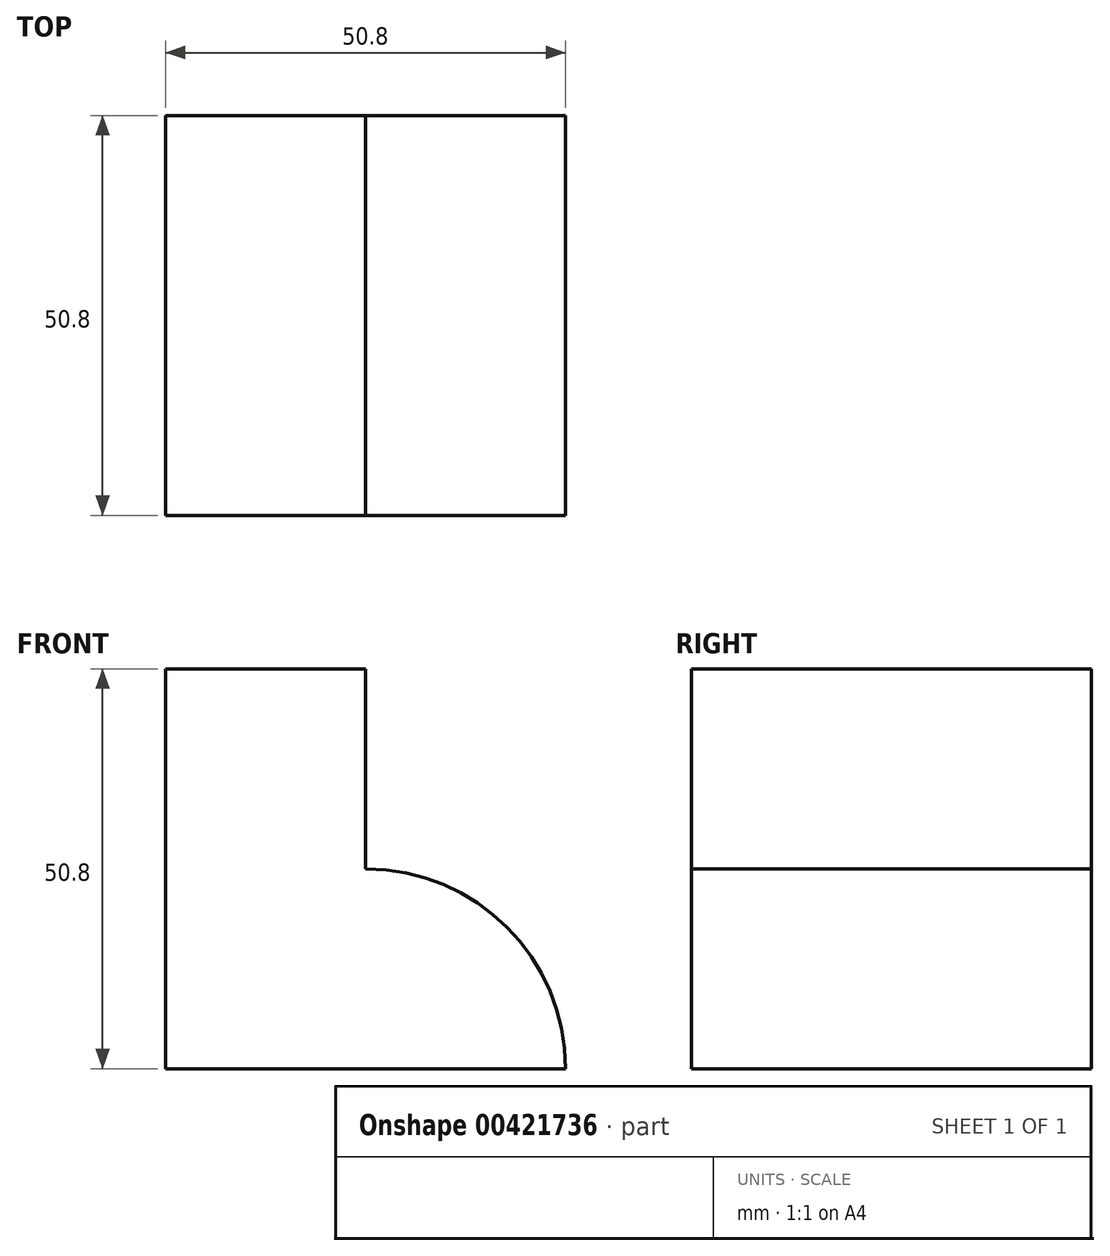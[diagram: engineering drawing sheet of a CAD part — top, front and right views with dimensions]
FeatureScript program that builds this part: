
annotation { "Feature Type Name" : "Feature", "Feature Type Description" : "" }
export const myFeature = defineFeature(function(context is Context, id is Id, definition is map)
    precondition{}
    {
        {
            var Q0;
            Q0=qCreatedBy(makeId("Front.planeOp"),FACE);
            var sketch = newSketch(context, id + "F0", { "sketchPlane" : qUnion([Q0])});
            skLineSegment(sketch, "E0", {"start": v(0, 0) * mm, "end": v(50.8, 0) * mm});
            skLineSegment(sketch, "E1", {"start": v(0, 0) * mm, "end": v(0, 50.8) * mm});
            skLineSegment(sketch, "E2", {"start": v(0, 50.8) * mm, "end": v(25.4, 50.8) * mm});
            skLineSegment(sketch, "E3", {"start": v(25.4, 50.8) * mm, "end": v(25.4, 25.4) * mm});
            skLineSegment(sketch, "E4", {"start": v(25.4, 25.4) * mm, "end": v(50.8, 0) * mm});
            skArc(sketch, "E5", {"start": v(50.8, 0) * mm, "mid": v(43.36, 17.96) * mm, "end": v(25.4, 25.4) * mm});
            skSolve(sketch);
        }
        {
            var Q0;
            Q0 = qSketchRegion(id + "F0", true);
            extrude(context, id + "F1", {"entities" : qUnion([Q0]), "depth" : 50.8 * mm});
        }
    });
